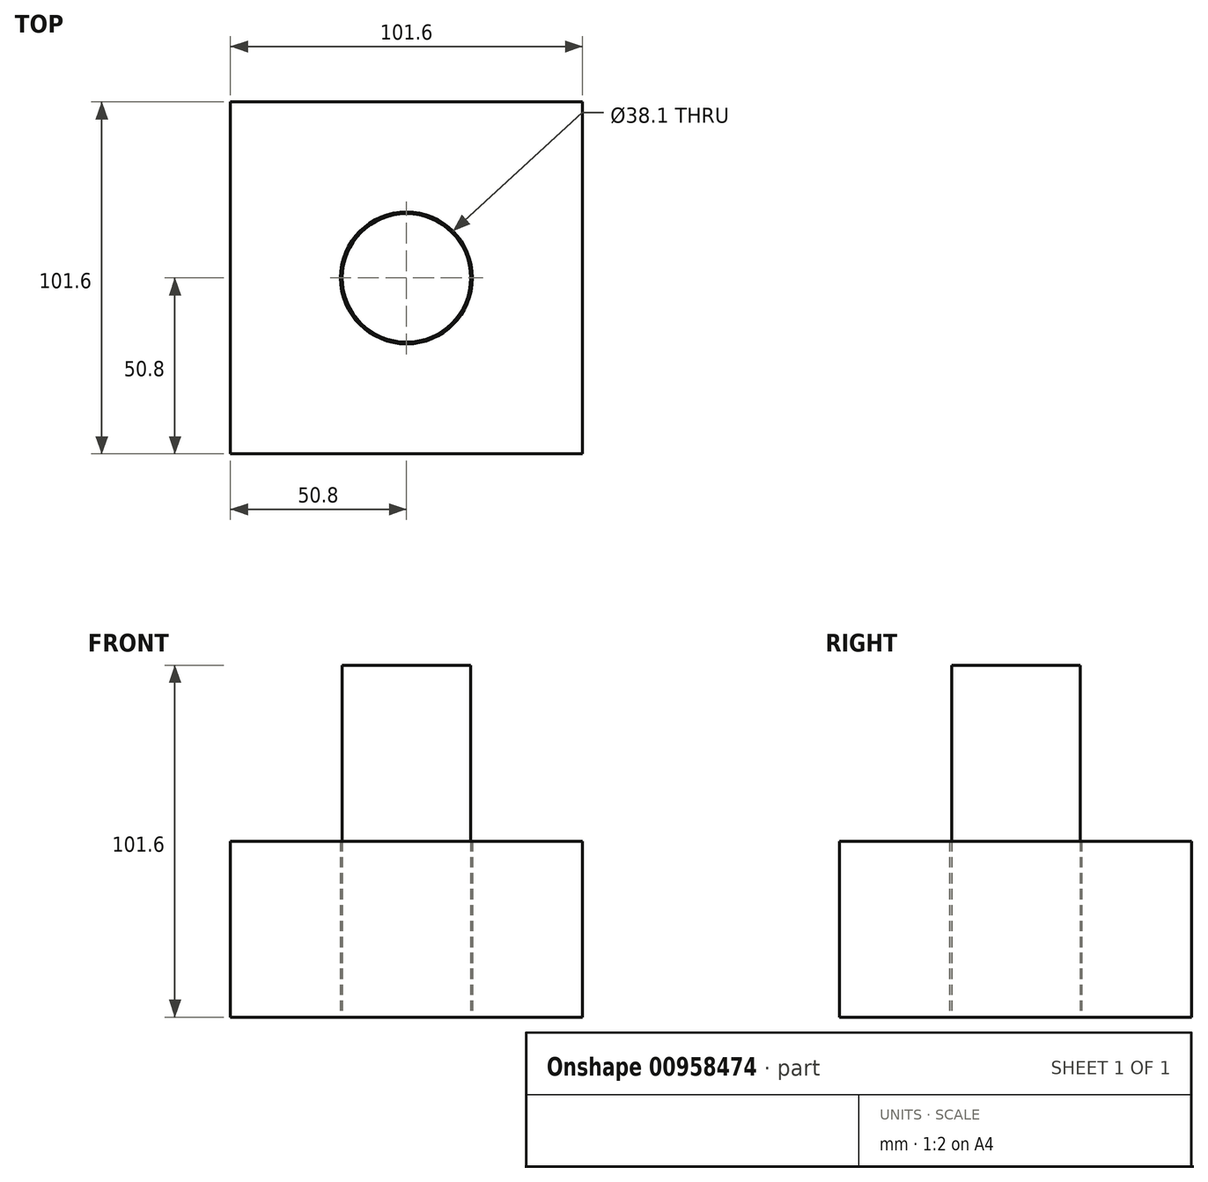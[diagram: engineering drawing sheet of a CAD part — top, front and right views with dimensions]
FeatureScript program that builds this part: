
annotation { "Feature Type Name" : "Feature", "Feature Type Description" : "" }
export const myFeature = defineFeature(function(context is Context, id is Id, definition is map)
    precondition{}
    {
        {
            var Q0;
            Q0=qCreatedBy(makeId("Top.planeOp"),FACE);
            var sketch = newSketch(context, id + "F0", { "sketchPlane" : qUnion([Q0])});
            skLineSegment(sketch, "E0.bottom", {"start": v(50.8, 50.8) * mm, "end": v(-50.8, 50.8) * mm});
            skLineSegment(sketch, "E0.top", {"start": v(50.8, -50.8) * mm, "end": v(-50.8, -50.8) * mm});
            skLineSegment(sketch, "E0.left", {"start": v(50.8, 50.8) * mm, "end": v(50.8, -50.8) * mm});
            skLineSegment(sketch, "E0.right", {"start": v(-50.8, 50.8) * mm, "end": v(-50.8, -50.8) * mm});
            skPoint(sketch, "E0.middle", {"position": v(0, 0) * mm});
            skCircle(sketch, "E1", {"center": v(0, 0) * mm, "radius": 19.05 * mm});
            skSolve(sketch);
        }
        {
            var Q0;
            Q0=makeQuery(id+"F0.imprint","IMPRINT",FACE,{"disambiguationData":[TD([[makeQuery(id+"F0.imprint","IMPRINT",EDGE,{"derivedFrom":sQuery(id+"F0.wireOp",EDGE,"E0.bottom")}),1.0]])]});
            extrude(context, id + "F1", {"entities" : qUnion([Q0]), "depth" : 50.8 * mm, "offsetDistance" : 25.4 * mm});
        }
        {
            var Q0;
            Q0=qCreatedBy(makeId("Top.planeOp"),FACE);
            var sketch = newSketch(context, id + "F2", { "sketchPlane" : qUnion([Q0])});
            skCircle(sketch, "E2", {"center": v(0, 0) * mm, "radius": 18.54 * mm});
            skSolve(sketch);
        }
        {
            var Q0;
            Q0 = qSketchRegion(id + "F2", true);
            extrude(context, id + "F3", {"entities" : qUnion([Q0]), "depth" : 101.6 * mm, "offsetDistance" : 25.4 * mm});
        }
    });
